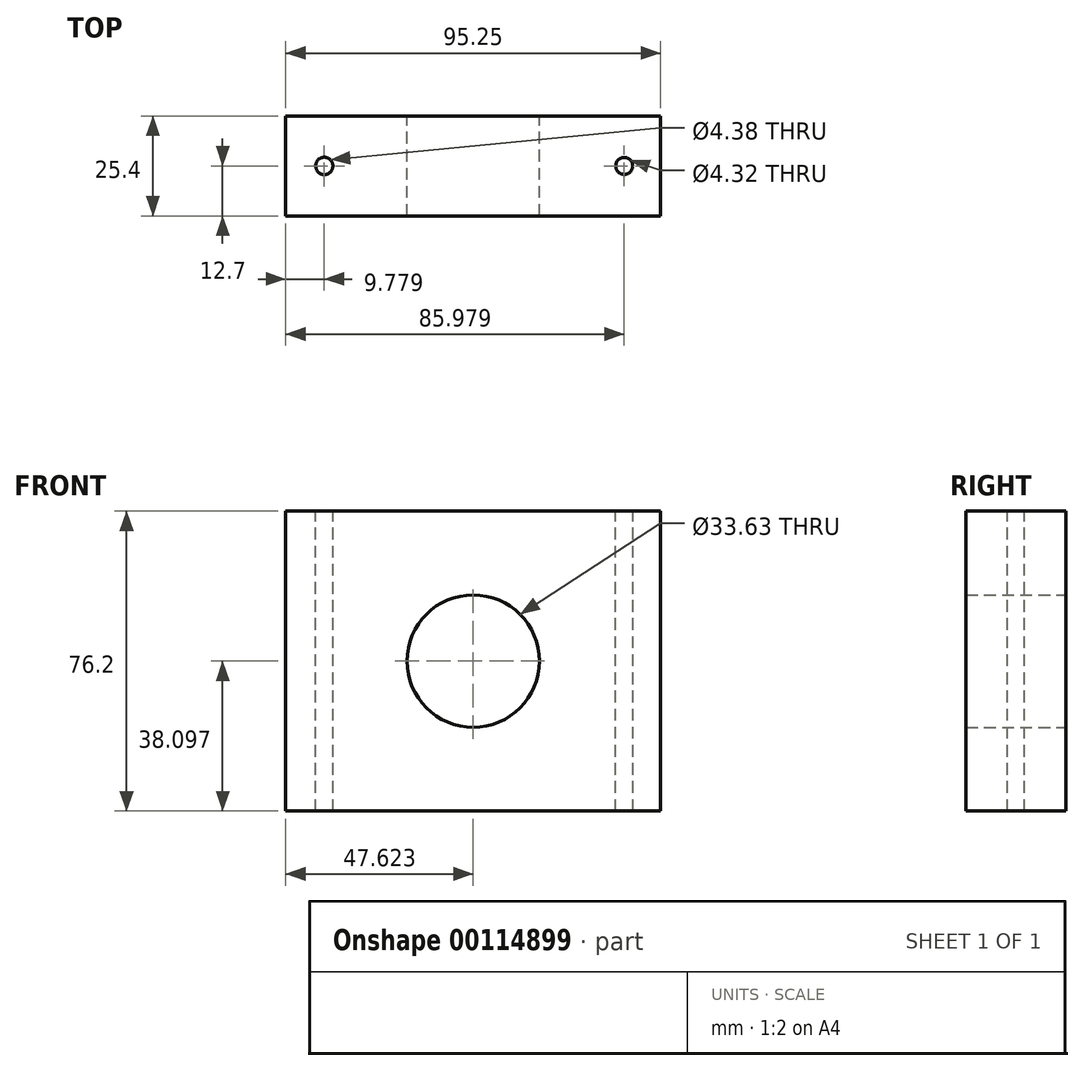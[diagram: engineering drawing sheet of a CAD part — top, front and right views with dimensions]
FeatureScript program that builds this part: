
annotation { "Feature Type Name" : "Feature", "Feature Type Description" : "" }
export const myFeature = defineFeature(function(context is Context, id is Id, definition is map)
    precondition{}
    {
        {
            var Q0;
            Q0=qCreatedBy(makeId("Front.planeOp"),FACE);
            var sketch = newSketch(context, id + "F0", { "sketchPlane" : qUnion([Q0])});
            skLineSegment(sketch, "E0.bottom", {"start": v(-57.2, 42.94) * mm, "end": v(38.06, 42.94) * mm});
            skLineSegment(sketch, "E0.top", {"start": v(-57.2, -33.26) * mm, "end": v(38.06, -33.26) * mm});
            skLineSegment(sketch, "E0.left", {"start": v(-57.2, 42.94) * mm, "end": v(-57.2, -33.26) * mm});
            skLineSegment(sketch, "E0.right", {"start": v(38.06, 42.94) * mm, "end": v(38.06, -33.26) * mm});
            skSolve(sketch);
        }
        {
            var Q0;
            Q0=makeQuery(id+"F0.imprint","IMPRINT",FACE,{"disambiguationData":[TD([[makeQuery(id+"F0.imprint","IMPRINT",EDGE,{"derivedFrom":sQuery(id+"F0.wireOp",EDGE,"E0.bottom")}),-1.0]])]});
            extrude(context, id + "F1", {"entities" : qUnion([Q0]), "depth" : 25.4 * mm});
        }
        {
            var Q0;
            Q0=makeQuery(id+"F1.opExtrude","SWEPT_FACE",FACE,{"disambiguationData":[OSD([sQuery(id+"F0.wireOp",EDGE,"E0.bottom")])]});
            var sketch = newSketch(context, id + "F2", { "sketchPlane" : qUnion([Q0])});
            skCircle(sketch, "E1", {"center": v(-47.41, -12.7) * mm, "radius": 2.2 * mm});
            skCircle(sketch, "E2", {"center": v(28.79, -12.7) * mm, "radius": 2.16 * mm});
            skSolve(sketch);
        }
        {
            var Q0;
            Q0=makeQuery(id+"F1.opExtrude","CAP_FACE",FACE,{"disambiguationData":[OSD([sQuery(id+"F0.wireOp",EDGE,"E0.bottom"),sQuery(id+"F0.wireOp",EDGE,"E0.top"),sQuery(id+"F0.wireOp",EDGE,"E0.left"),sQuery(id+"F0.wireOp",EDGE,"E0.right")])],"isStart":true});
            var sketch = newSketch(context, id + "F3", { "sketchPlane" : qUnion([Q0])});
            skLineSegment(sketch, "E3", {"start": v(9.57, 42.94) * mm, "end": v(9.57, -33.26) * mm});
            skLineSegment(sketch, "E4", {"start": v(-38.06, 4.84) * mm, "end": v(57.2, 4.84) * mm});
            skCircle(sketch, "E5", {"center": v(9.57, 4.84) * mm, "radius": 16.81 * mm});
            skSolve(sketch);
        }
        {
            var Q0;
            Q0 = qSketchRegion(id + "F3", true);
            extrude(context, id + "F4", {"entities" : qUnion([Q0]), "operationType" : NewBodyOperationType.REMOVE, "endBound" : BoundingType.THROUGH_ALL, "oppositeDirection" : true, "depth" : 25.4 * mm});
        }
        {
            var Q0;
            Q0=makeQuery(id+"F2.imprint","IMPRINT",FACE,{"disambiguationData":[TD([[makeQuery(id+"F2.imprint","IMPRINT",EDGE,{"derivedFrom":sQuery(id+"F2.wireOp",EDGE,"E2")}),1.0]])]});
            var Q1;
            Q1=makeQuery(id+"F2.imprint","IMPRINT",FACE,{"disambiguationData":[TD([[makeQuery(id+"F2.imprint","IMPRINT",EDGE,{"derivedFrom":sQuery(id+"F2.wireOp",EDGE,"E1")}),1.0]])]});
            extrude(context, id + "F5", {"entities" : qUnion([Q0, Q1]), "operationType" : NewBodyOperationType.REMOVE, "endBound" : BoundingType.THROUGH_ALL, "oppositeDirection" : true, "depth" : 25.4 * mm});
        }
    });
